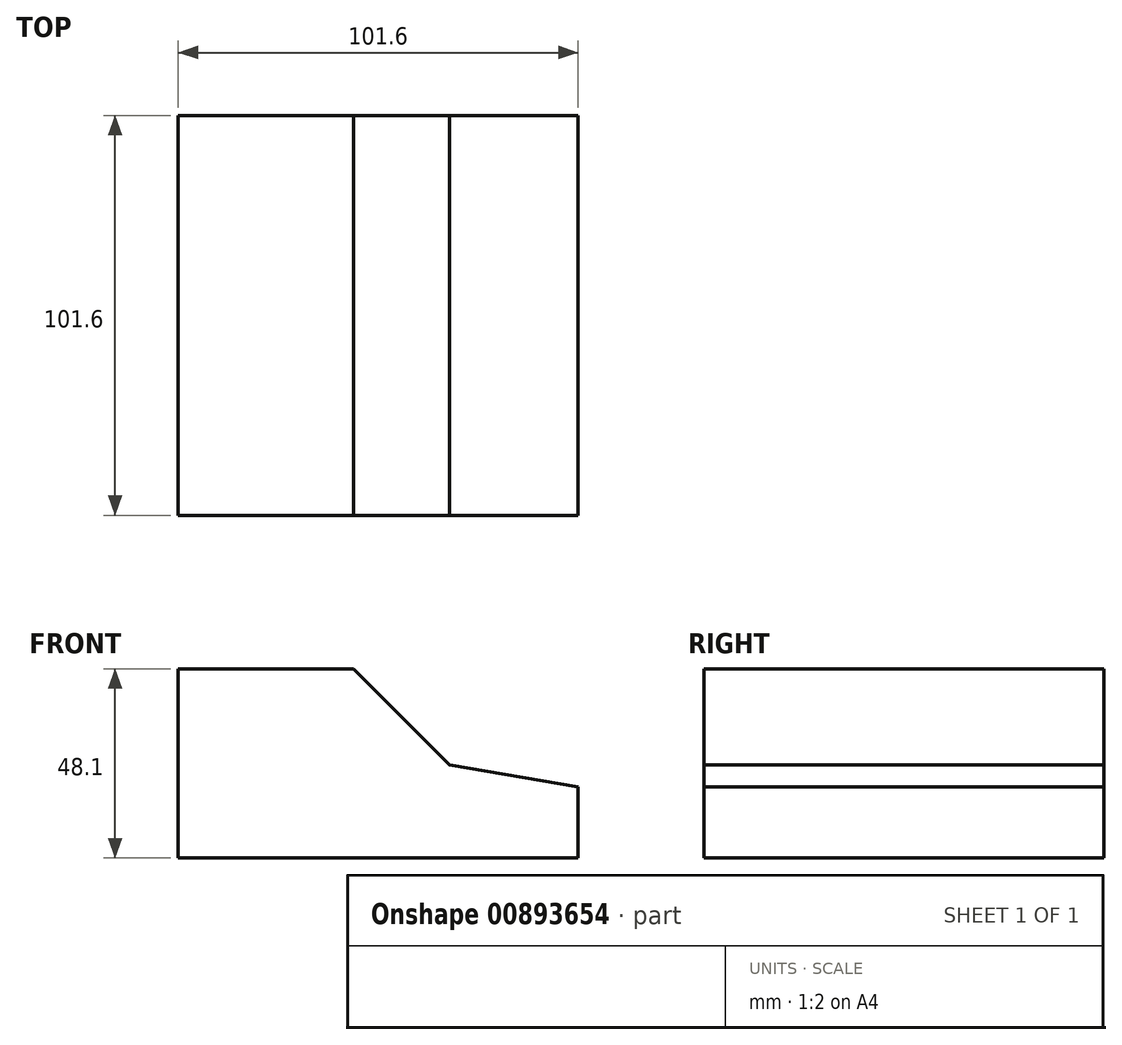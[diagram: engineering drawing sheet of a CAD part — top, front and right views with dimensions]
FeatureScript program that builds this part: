
annotation { "Feature Type Name" : "Feature", "Feature Type Description" : "" }
export const myFeature = defineFeature(function(context is Context, id is Id, definition is map)
    precondition{}
    {
        {
            var Q0;
            Q0=qCreatedBy(makeId("Front.planeOp"),FACE);
            var sketch = newSketch(context, id + "F0", { "sketchPlane" : qUnion([Q0])});
            skLineSegment(sketch, "E0", {"start": v(-31.95, -18.05) * mm, "end": v(-31.95, 30.05) * mm});
            skLineSegment(sketch, "E1", {"start": v(-31.95, 30.05) * mm, "end": v(12.55, 30.05) * mm});
            skLineSegment(sketch, "E2", {"start": v(12.55, 30.05) * mm, "end": v(37.01, 5.58) * mm});
            skLineSegment(sketch, "E3", {"start": v(37.01, 5.58) * mm, "end": v(69.65, 0) * mm});
            skLineSegment(sketch, "E4", {"start": v(69.65, 0) * mm, "end": v(69.65, -18.05) * mm});
            skLineSegment(sketch, "E5", {"start": v(69.65, -18.05) * mm, "end": v(-31.95, -18.05) * mm});
            skSolve(sketch);
        }
        {
            var Q0;
            Q0=makeQuery(id+"F0.imprint","IMPRINT",FACE,{"disambiguationData":[TD([[makeQuery(id+"F0.imprint","IMPRINT",EDGE,{"derivedFrom":sQuery(id+"F0.wireOp",EDGE,"E0")}),-1.0]])]});
            extrude(context, id + "F1", {"entities" : qUnion([Q0]), "depth" : 101.6 * mm, "offsetDistance" : 25.4 * mm});
        }
    });
